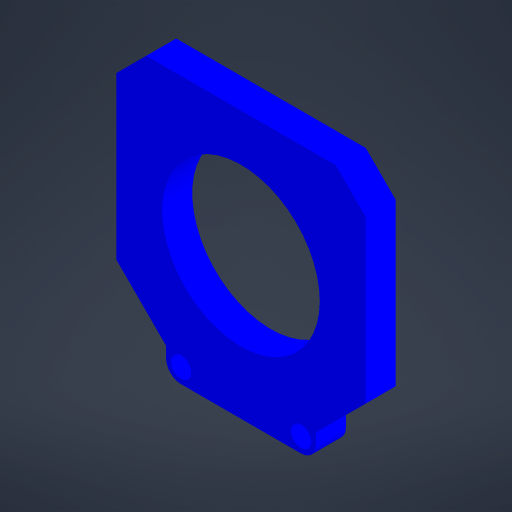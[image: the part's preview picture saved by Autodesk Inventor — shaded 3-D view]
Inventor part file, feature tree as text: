
AUTODESK INVENTOR PART (.ipt)
format: ipt  version: 2023.4 (Build 274418000, 418)  size: 209,408 bytes
history: native  units: mm
features: other x3, extrude x1, reference x1
ambient origin geometry x8: Origin, YZ Plane, XZ Plane, XY Plane, X Axis, Y Axis, Z Axis, Center Point
bodies: Solid1 (feature_tree)
feature tree (5):
  extrude  "Extrusion1"  Depth=5.0mm
  reference  "Reference2"
  other  "<path>\Projects\Project Protocube\Protocube\CAD, STL, OBJ Files\1 CAD\Cube 1x1 V5.iam"
  other  "Cube 1x1 V5.iam"
  other  "Cube 1x1 Bottom V5 Closed Slotted:1"
note: 1 file-system path scrubbed to <path> (originals preserved in map.json)
